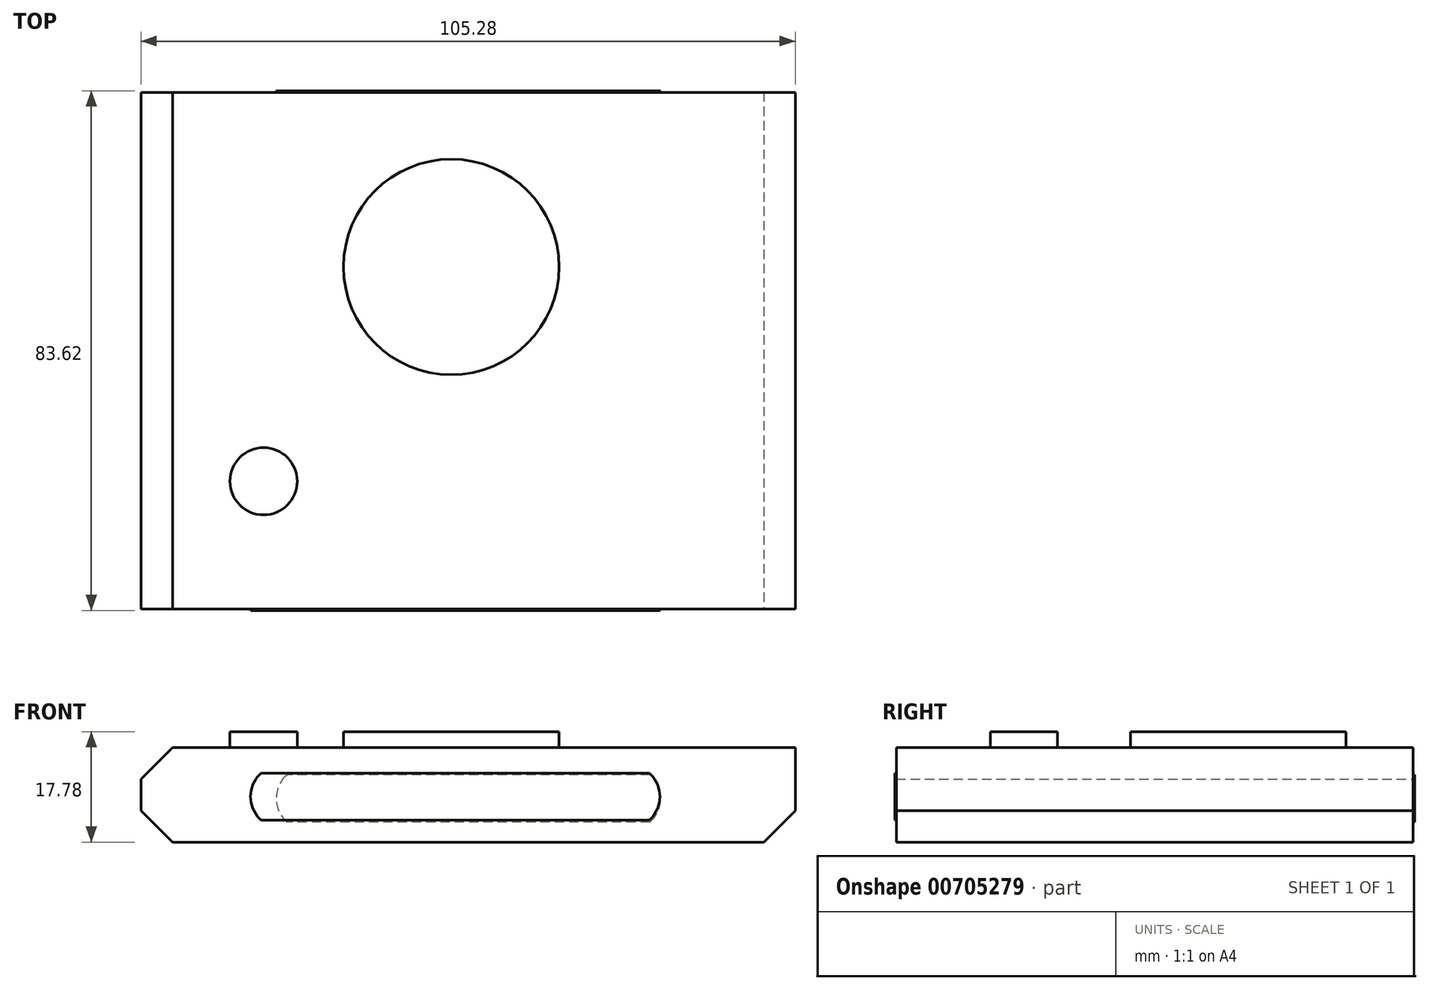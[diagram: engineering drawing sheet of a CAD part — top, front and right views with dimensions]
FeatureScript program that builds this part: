
annotation { "Feature Type Name" : "Feature", "Feature Type Description" : "" }
export const myFeature = defineFeature(function(context is Context, id is Id, definition is map)
    precondition{}
    {
        {
            var Q0;
            Q0=qCreatedBy(makeId("Top.planeOp"),FACE);
            var sketch = newSketch(context, id + "F0", { "sketchPlane" : qUnion([Q0])});
            skLineSegment(sketch, "E0.bottom", {"start": v(-35.68, 28.1) * mm, "end": v(69.6, 28.1) * mm});
            skLineSegment(sketch, "E0.top", {"start": v(-35.68, -55.02) * mm, "end": v(69.6, -55.02) * mm});
            skLineSegment(sketch, "E0.left", {"start": v(-35.68, 28.1) * mm, "end": v(-35.68, -55.02) * mm});
            skLineSegment(sketch, "E0.right", {"start": v(69.6, 28.1) * mm, "end": v(69.6, -55.02) * mm});
            skSolve(sketch);
        }
        {
            var Q0;
            Q0 = qSketchRegion(id + "F0", true);
            extrude(context, id + "F1", {"entities" : qUnion([Q0]), "depth" : 15.24 * mm, "offsetDistance" : 25.4 * mm});
        }
        {
            var Q0;
            Q0=makeQuery(id+"F1.opExtrude","CAP_EDGE",EDGE,{"disambiguationData":[OSD([sQuery(id+"F0.wireOp",EDGE,"E0.left")])],"isStart":false});
            var Q1;
            Q1=makeQuery(id+"F1.opExtrude","CAP_EDGE",EDGE,{"disambiguationData":[OSD([sQuery(id+"F0.wireOp",EDGE,"E0.left")])],"isStart":true});
            chamfer(context, id + "F2", {"entities" : qUnion([Q0, Q1]), "width" : 5.08 * mm, "tangentPropagation" : true});
        }
        {
            var Q0;
            Q0=makeQuery(id+"F1.opExtrude","CAP_EDGE",EDGE,{"disambiguationData":[OSD([sQuery(id+"F0.wireOp",EDGE,"E0.right")])],"isStart":true});
            chamfer(context, id + "F3", {"entities" : qUnion([Q0]), "width" : 5.08 * mm, "tangentPropagation" : true});
        }
        {
            var Q0;
            Q0=makeQuery(id+"F1.opExtrude","CAP_FACE",FACE,{"disambiguationData":[OSD([sQuery(id+"F0.wireOp",EDGE,"E0.bottom"),sQuery(id+"F0.wireOp",EDGE,"E0.top"),sQuery(id+"F0.wireOp",EDGE,"E0.left"),sQuery(id+"F0.wireOp",EDGE,"E0.right")])],"isStart":false});
            var sketch = newSketch(context, id + "F4", { "sketchPlane" : qUnion([Q0])});
            skCircle(sketch, "E1", {"center": v(14.24, 0) * mm, "radius": 17.34 * mm});
            skCircle(sketch, "E2", {"center": v(-15.96, -34.48) * mm, "radius": 5.4 * mm});
            skSolve(sketch);
        }
        {
            var Q0;
            Q0 = qSketchRegion(id + "F4", true);
            extrude(context, id + "F5", {"entities" : qUnion([Q0]), "operationType" : NewBodyOperationType.ADD, "depth" : 2.54 * mm, "offsetDistance" : 25.4 * mm});
        }
        {
            var Q0;
            Q0=makeQuery(id+"F1.opExtrude","SWEPT_FACE",FACE,{"disambiguationData":[OSD([sQuery(id+"F0.wireOp",EDGE,"E0.bottom")])]});
            var sketch = newSketch(context, id + "F6", { "sketchPlane" : qUnion([Q0])});
            skLineSegment(sketch, "E3.bottom", {"start": v(-51.28, 10.86) * mm, "end": v(17.28, 10.86) * mm});
            skLineSegment(sketch, "E3.top", {"start": v(-51.28, 3.2) * mm, "end": v(17.28, 3.2) * mm});
            skLineSegment(sketch, "E3.left", {"start": v(-51.28, 10.86) * mm, "end": v(-51.28, 3.2) * mm});
            skLineSegment(sketch, "E3.right", {"start": v(17.28, 10.86) * mm, "end": v(17.28, 3.2) * mm});
            skSolve(sketch);
        }
        {
            var Q0;
            Q0 = qSketchRegion(id + "F6", true);
            extrude(context, id + "F7", {"entities" : qUnion([Q0]), "operationType" : NewBodyOperationType.ADD, "depth" : 0.25 * mm, "offsetDistance" : 25.4 * mm});
        }
        {
            var Q0;
            Q0=makeQuery(id+"F1.opExtrude","SWEPT_FACE",FACE,{"disambiguationData":[OSD([sQuery(id+"F0.wireOp",EDGE,"E0.top")])]});
            var sketch = newSketch(context, id + "F8", { "sketchPlane" : qUnion([Q0])});
            skLineSegment(sketch, "E4.bottom", {"start": v(-21.45, 11.1) * mm, "end": v(51.2, 11.1) * mm});
            skLineSegment(sketch, "E4.top", {"start": v(-21.45, 3.54) * mm, "end": v(51.2, 3.54) * mm});
            skLineSegment(sketch, "E4.left", {"start": v(-21.45, 11.1) * mm, "end": v(-21.45, 3.54) * mm});
            skLineSegment(sketch, "E4.right", {"start": v(51.2, 11.1) * mm, "end": v(51.2, 3.54) * mm});
            skSolve(sketch);
        }
        {
            var Q0;
            Q0 = qSketchRegion(id + "F8", true);
            extrude(context, id + "F9", {"entities" : qUnion([Q0]), "operationType" : NewBodyOperationType.ADD, "depth" : 0.25 * mm, "offsetDistance" : 25.4 * mm});
        }
        {
            var Q0;
            Q0=makeQuery(id+"F9.opExtrude","SWEPT_EDGE",EDGE,{"disambiguationData":[OSD([sQuery(id+"F8.wireOp",EDGE,"E4.top"),sQuery(id+"F8.wireOp",EDGE,"E4.right")])]});
            var Q1;
            Q1=makeQuery(id+"F9.opExtrude","SWEPT_EDGE",EDGE,{"disambiguationData":[OSD([sQuery(id+"F8.wireOp",EDGE,"E4.bottom"),sQuery(id+"F8.wireOp",EDGE,"E4.right")])]});
            var Q2;
            Q2=makeQuery(id+"F9.opExtrude","SWEPT_EDGE",EDGE,{"disambiguationData":[OSD([sQuery(id+"F8.wireOp",EDGE,"E4.bottom"),sQuery(id+"F8.wireOp",EDGE,"E4.left")])]});
            var Q3;
            Q3=makeQuery(id+"F9.opExtrude","SWEPT_EDGE",EDGE,{"disambiguationData":[OSD([sQuery(id+"F8.wireOp",EDGE,"E4.top"),sQuery(id+"F8.wireOp",EDGE,"E4.left")])]});
            chamfer(context, id + "F10", {"entities" : qUnion([Q0, Q1, Q2, Q3]), "width" : 5.08 * mm, "tangentPropagation" : true});
        }
        {
            var Q0;
            {var subQ0=sQuery(id+"F8.wireOp",EDGE,"E4.left");Q0=makeQuery(id+"F10.opChamfer","BLEND_EDGE",EDGE,{"blendedFrom":[makeQuery(id+"F9.opExtrude","SWEPT_EDGE",EDGE,{"disambiguationData":[OSD([sQuery(id+"F8.wireOp",EDGE,"E4.bottom"),subQ0])]}),makeQuery(id+"F9.opExtrude","SWEPT_EDGE",EDGE,{"disambiguationData":[OSD([sQuery(id+"F8.wireOp",EDGE,"E4.top"),subQ0])]})],"blendedInto":[]});}
            var Q1;
            {var subQ0=sQuery(id+"F8.wireOp",EDGE,"E4.right");Q1=makeQuery(id+"F10.opChamfer","BLEND_EDGE",EDGE,{"blendedFrom":[makeQuery(id+"F9.opExtrude","SWEPT_EDGE",EDGE,{"disambiguationData":[OSD([sQuery(id+"F8.wireOp",EDGE,"E4.bottom"),subQ0])]}),makeQuery(id+"F9.opExtrude","SWEPT_EDGE",EDGE,{"disambiguationData":[OSD([sQuery(id+"F8.wireOp",EDGE,"E4.top"),subQ0])]})],"blendedInto":[]});}
            fillet(context, id + "F11", {"entities" : qUnion([Q0, Q1]), "radius" : 5.08 * mm, "tangentPropagation" : true, "allowEdgeOverflow" : false});
        }
        {
            var Q0;
            Q0=makeQuery(id+"F7.opExtrude","SWEPT_EDGE",EDGE,{"disambiguationData":[OSD([sQuery(id+"F6.wireOp",EDGE,"E3.bottom"),sQuery(id+"F6.wireOp",EDGE,"E3.left")])]});
            var Q1;
            Q1=makeQuery(id+"F7.opExtrude","SWEPT_EDGE",EDGE,{"disambiguationData":[OSD([sQuery(id+"F6.wireOp",EDGE,"E3.top"),sQuery(id+"F6.wireOp",EDGE,"E3.left")])]});
            var Q2;
            Q2=makeQuery(id+"F7.opExtrude","SWEPT_EDGE",EDGE,{"disambiguationData":[OSD([sQuery(id+"F6.wireOp",EDGE,"E3.top"),sQuery(id+"F6.wireOp",EDGE,"E3.right")])]});
            var Q3;
            Q3=makeQuery(id+"F7.opExtrude","SWEPT_EDGE",EDGE,{"disambiguationData":[OSD([sQuery(id+"F6.wireOp",EDGE,"E3.bottom"),sQuery(id+"F6.wireOp",EDGE,"E3.right")])]});
            chamfer(context, id + "F12", {"entities" : qUnion([Q0, Q1, Q2, Q3]), "width" : 5.08 * mm, "tangentPropagation" : true});
        }
        {
            var Q0;
            {var subQ0=sQuery(id+"F6.wireOp",EDGE,"E3.right");Q0=makeQuery(id+"F12.opChamfer","BLEND_EDGE",EDGE,{"blendedFrom":[makeQuery(id+"F7.opExtrude","SWEPT_EDGE",EDGE,{"disambiguationData":[OSD([sQuery(id+"F6.wireOp",EDGE,"E3.bottom"),subQ0])]}),makeQuery(id+"F7.opExtrude","SWEPT_EDGE",EDGE,{"disambiguationData":[OSD([sQuery(id+"F6.wireOp",EDGE,"E3.top"),subQ0])]})],"blendedInto":[]});}
            var Q1;
            {var subQ0=sQuery(id+"F6.wireOp",EDGE,"E3.left");Q1=makeQuery(id+"F12.opChamfer","BLEND_EDGE",EDGE,{"blendedFrom":[makeQuery(id+"F7.opExtrude","SWEPT_EDGE",EDGE,{"disambiguationData":[OSD([sQuery(id+"F6.wireOp",EDGE,"E3.bottom"),subQ0])]}),makeQuery(id+"F7.opExtrude","SWEPT_EDGE",EDGE,{"disambiguationData":[OSD([sQuery(id+"F6.wireOp",EDGE,"E3.top"),subQ0])]})],"blendedInto":[]});}
            fillet(context, id + "F13", {"entities" : qUnion([Q0, Q1]), "radius" : 5.08 * mm, "tangentPropagation" : true, "allowEdgeOverflow" : false});
        }
    });
